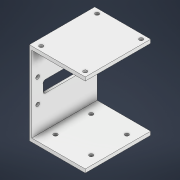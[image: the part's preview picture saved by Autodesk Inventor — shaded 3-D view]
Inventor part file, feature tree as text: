
AUTODESK INVENTOR PART (.ipt)
format: ipt  version: 2021 (Build 250183000, 183)  size: 381,952 bytes
history: native  units: mm
features: extrude x6, sketch x5, fillet x1
ambient origin geometry x8: Origin, YZ Plane, XZ Plane, XY Plane, X Axis, Y Axis, Z Axis, Center Point
bodies: Volumenkörper1 (feature_tree)
feature tree (12):
  extrude  "Extrusion1"  Depth=55.0mm
  extrude  "Extrusion2"  Depth=3.0mm
  extrude  "Extrusion3"  Depth=45.0mm TaperAngle=0.0deg
  extrude  "Extrusion4"  Depth=3.2mm
  sketch  "Skizze7"  dims[d44=3.2mm d47=3.2mm d50=45.0mm d51=0.0mm d52=3.2mm d53=3.2mm d63=3.2mm d65=3.2mm d66=45.0mm d67=0.0mm d69=6.0mm d70=4.0mm d71=4.0mm d72=6.0mm d73=4.0mm d74=4.0mm d75=4.0mm d76=4.0mm d84=15.0mm d86=9.5mm d87=9.5mm d88=15.0mm d89=15.0mm d90=7.5mm d91=7.5mm d92=15.0mm d93=3.2mm d95=5.0mm d96=3.2mm d97=5.0mm d99=3.2mm d100=5.0mm d101=20.0mm d102=3.2mm d103=5.0mm d104=20.0mm d105=10.0mm d106=0.0mm d107=36.0mm d108=10.0mm d111=10.0mm d112=10.0mm d113=10.0mm d114=0.0mm d115=2.0mm]
  extrude  "Extrusion5"  Depth=2.0mm
  extrude  "Extrusion6"  Depth=45.0mm TaperAngle=0.0deg
  fillet  "Rundung1"  Radius=3.2mm
  sketch  "Skizze2"  dims[d5=70.0mm d6=55.0mm]
  sketch  "Skizze3"  dims[d7=2.0mm d8=0.0mm d9=3.0mm]
  sketch  "Skizze5"  dims[d10=3.0mm d11=45.0mm d12=0.0mm]
  sketch  "Skizze6"  dims[d38=3.2mm d41=3.2mm]
